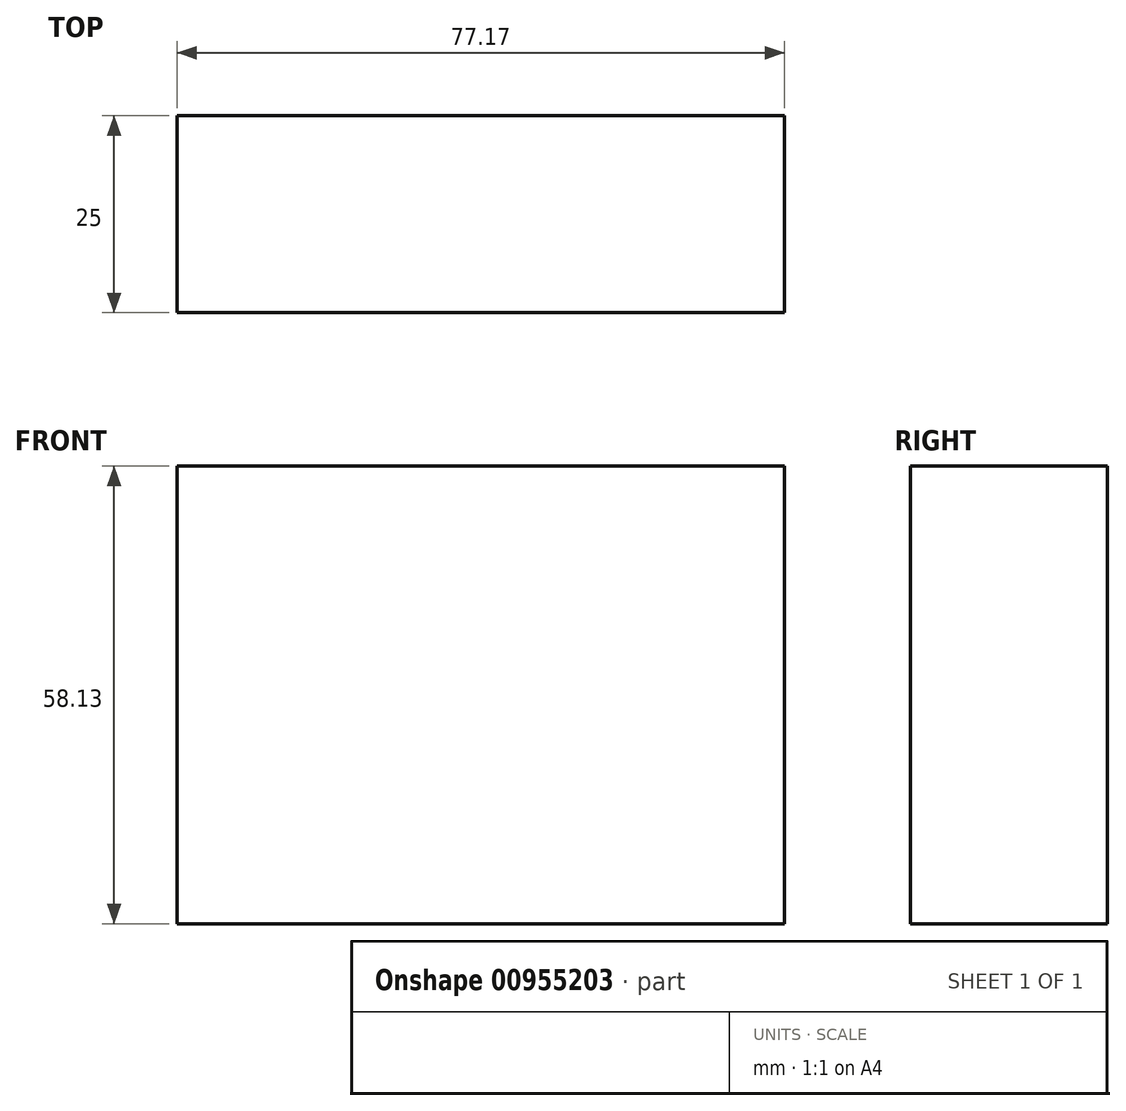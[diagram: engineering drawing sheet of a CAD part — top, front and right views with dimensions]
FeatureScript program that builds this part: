
annotation { "Feature Type Name" : "Feature", "Feature Type Description" : "" }
export const myFeature = defineFeature(function(context is Context, id is Id, definition is map)
    precondition{}
    {
        {
            var Q0;
            Q0=qCreatedBy(makeId("Front.planeOp"),FACE);
            var sketch = newSketch(context, id + "F0", { "sketchPlane" : qUnion([Q0])});
            skLineSegment(sketch, "E0.bottom", {"start": v(-47.16, 58.13) * mm, "end": v(30.01, 58.13) * mm});
            skLineSegment(sketch, "E0.top", {"start": v(-47.16, 0) * mm, "end": v(30.01, 0) * mm});
            skLineSegment(sketch, "E0.left", {"start": v(-47.16, 58.13) * mm, "end": v(-47.16, 0) * mm});
            skLineSegment(sketch, "E0.right", {"start": v(30.01, 58.13) * mm, "end": v(30.01, 0) * mm});
            skSolve(sketch);
        }
        {
            var Q0;
            Q0 = qSketchRegion(id + "F0", true);
            extrude(context, id + "F1", {"entities" : qUnion([Q0]), "depth" : 25 * mm, "offsetDistance" : 25 * mm});
        }
    });
